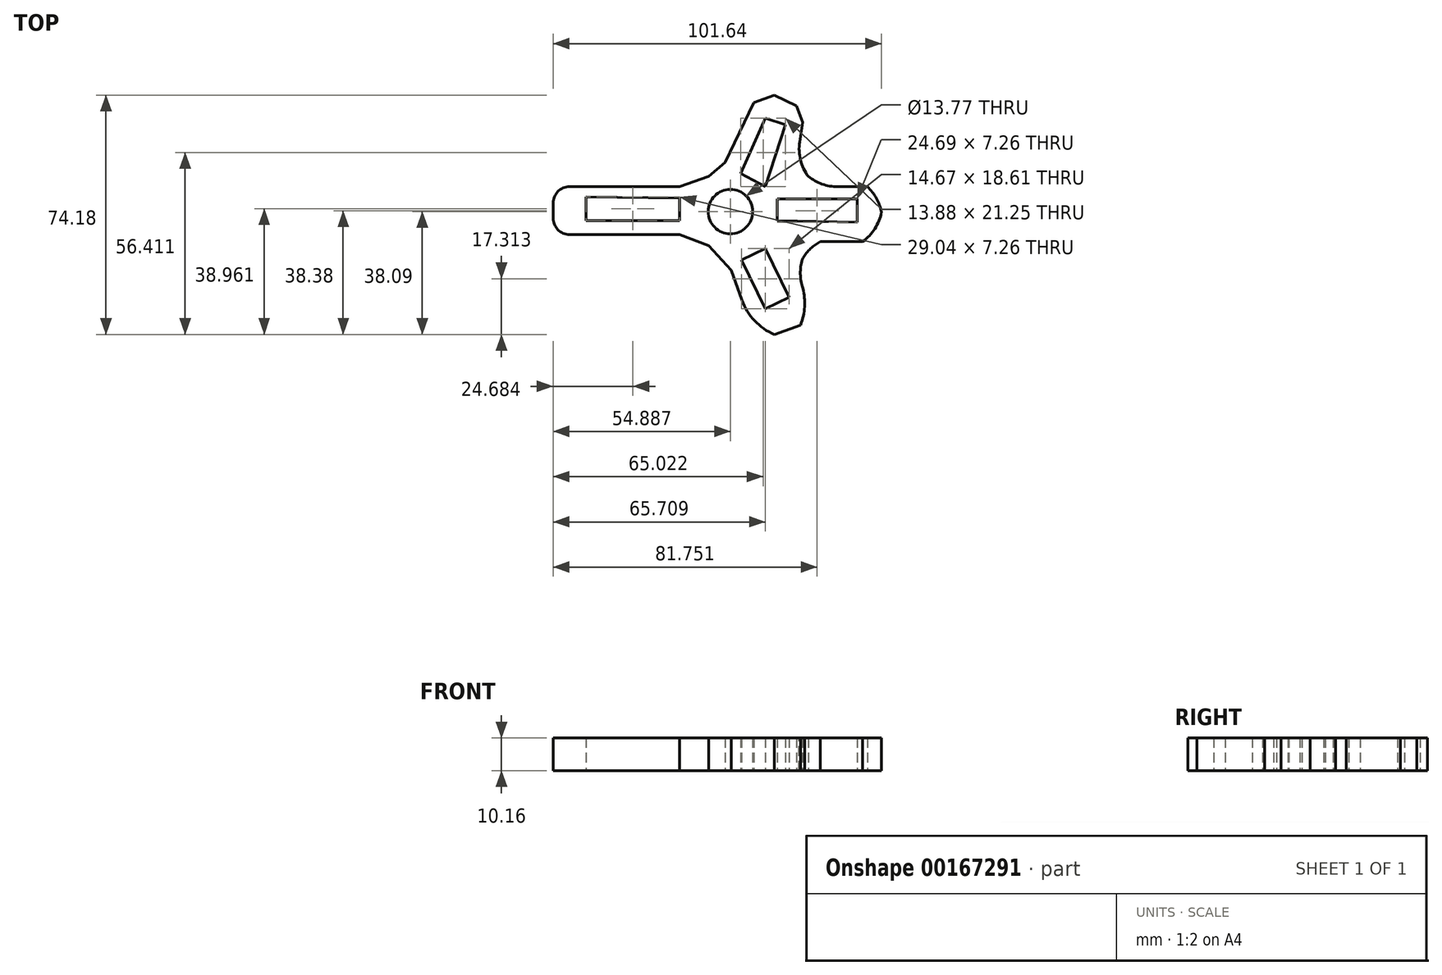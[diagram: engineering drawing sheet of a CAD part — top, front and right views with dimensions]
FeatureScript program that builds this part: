
annotation { "Feature Type Name" : "Feature", "Feature Type Description" : "" }
export const myFeature = defineFeature(function(context is Context, id is Id, definition is map)
    precondition{}
    {
        {
            var Q0;
            Q0=qCreatedBy(makeId("Top.planeOp"),FACE);
            var sketch = newSketch(context, id + "F0", { "sketchPlane" : qUnion([Q0])});
            skLineSegment(sketch, "E0", {"start": v(5.52, 10.9) * mm, "end": v(-3.49, 7.7) * mm});
            skLineSegment(sketch, "E1", {"start": v(-3.49, 7.7) * mm, "end": v(-42.7, 7.7) * mm});
            skLineSegment(sketch, "E2", {"start": v(-42.7, 7.7) * mm, "end": v(-42.7, -7.12) * mm});
            skLineSegment(sketch, "E3", {"start": v(-42.7, -7.12) * mm, "end": v(-3.49, -7.12) * mm});
            skLineSegment(sketch, "E4", {"start": v(-3.49, -7.12) * mm, "end": v(5.52, -10.6) * mm});
            skLineSegment(sketch, "E5", {"start": v(5.52, -10.6) * mm, "end": v(12.49, -18.15) * mm});
            skLineSegment(sketch, "E6", {"start": v(12.49, -18.15) * mm, "end": v(19.56, -38.09) * mm});
            skLineSegment(sketch, "E7", {"start": v(19.56, -38.09) * mm, "end": v(25.85, -38.09) * mm});
            skLineSegment(sketch, "E8", {"start": v(25.85, -38.09) * mm, "end": v(33.86, -35.24) * mm});
            skLineSegment(sketch, "E9", {"start": v(33.86, -35.24) * mm, "end": v(36.3, -28.32) * mm});
            skLineSegment(sketch, "E10", {"start": v(36.3, -28.32) * mm, "end": v(32.7, -18.15) * mm});
            skLineSegment(sketch, "E11", {"start": v(32.7, -18.15) * mm, "end": v(36.3, -10.6) * mm});
            skLineSegment(sketch, "E12", {"start": v(36.3, -10.6) * mm, "end": v(40.05, -9.27) * mm});
            skLineSegment(sketch, "E13", {"start": v(40.05, -9.27) * mm, "end": v(53.15, -9.27) * mm});
            skLineSegment(sketch, "E14", {"start": v(53.15, -9.27) * mm, "end": v(59.22, -7.12) * mm});
            skLineSegment(sketch, "E15", {"start": v(59.22, -7.12) * mm, "end": v(59.22, 5.37) * mm});
            skLineSegment(sketch, "E16", {"start": v(59.22, 5.37) * mm, "end": v(54.6, 7.7) * mm});
            skLineSegment(sketch, "E17", {"start": v(54.6, 7.7) * mm, "end": v(40.05, 7.7) * mm});
            skLineSegment(sketch, "E18", {"start": v(40.05, 7.7) * mm, "end": v(36.3, 10.9) * mm});
            skLineSegment(sketch, "E19", {"start": v(36.3, 10.9) * mm, "end": v(32.7, 15.25) * mm});
            skLineSegment(sketch, "E20", {"start": v(32.7, 15.25) * mm, "end": v(34.5, 27.73) * mm});
            skPoint(sketch, "E20.endSnap0", {"position": v(34.5, -23.23) * mm});
            skLineSegment(sketch, "E21", {"start": v(34.5, 27.73) * mm, "end": v(32.7, 32.82) * mm});
            skLineSegment(sketch, "E22", {"start": v(32.7, 32.82) * mm, "end": v(25.85, 36.09) * mm});
            skLineSegment(sketch, "E23", {"start": v(25.85, 36.09) * mm, "end": v(19.48, 33.83) * mm});
            skLineSegment(sketch, "E24", {"start": v(19.48, 33.83) * mm, "end": v(10.6, 15.25) * mm});
            skLineSegment(sketch, "E25", {"start": v(10.6, 15.25) * mm, "end": v(5.52, 10.9) * mm});
            skLineSegment(sketch, "E26", {"start": v(-32.53, 4.5) * mm, "end": v(-32.53, -2.76) * mm});
            skLineSegment(sketch, "E27", {"start": v(-32.53, -2.76) * mm, "end": v(-3.49, -2.76) * mm});
            skLineSegment(sketch, "E28", {"start": v(-3.49, -2.76) * mm, "end": v(-3.49, 4.21) * mm});
            skLineSegment(sketch, "E29", {"start": v(-3.49, 4.21) * mm, "end": v(-32.53, 4.5) * mm});
            skLineSegment(sketch, "E30", {"start": v(15.4, 11.76) * mm, "end": v(22.94, 7.7) * mm});
            skLineSegment(sketch, "E31", {"start": v(22.94, 7.7) * mm, "end": v(29.27, 26.86) * mm});
            skPoint(sketch, "E31.endSnap0", {"position": v(29.27, 34.45) * mm});
            skLineSegment(sketch, "E32", {"start": v(29.27, 26.86) * mm, "end": v(22.96, 28.95) * mm});
            skLineSegment(sketch, "E33", {"start": v(22.96, 28.95) * mm, "end": v(15.4, 11.76) * mm});
            skLineSegment(sketch, "E34", {"start": v(26.72, -2.76) * mm, "end": v(26.72, 3.92) * mm});
            skLineSegment(sketch, "E35", {"start": v(26.72, 3.92) * mm, "end": v(51.4, 3.92) * mm});
            skLineSegment(sketch, "E36", {"start": v(51.4, 3.92) * mm, "end": v(51.4, -3.34) * mm});
            skLineSegment(sketch, "E37", {"start": v(51.4, -3.34) * mm, "end": v(26.72, -2.76) * mm});
            skLineSegment(sketch, "E38", {"start": v(22.94, -11.47) * mm, "end": v(15.68, -14.96) * mm});
            skLineSegment(sketch, "E39", {"start": v(15.68, -14.96) * mm, "end": v(22.94, -30.08) * mm});
            skLineSegment(sketch, "E40", {"start": v(22.94, -30.08) * mm, "end": v(30.35, -26.52) * mm});
            skLineSegment(sketch, "E41", {"start": v(30.35, -26.52) * mm, "end": v(22.94, -11.47) * mm});
            skCircle(sketch, "E42", {"center": v(12.2, 0) * mm, "radius": 6.89 * mm});
            skSolve(sketch);
        }
        {
            var Q0;
            Q0 = qSketchRegion(id + "F0", true);
            extrude(context, id + "F1", {"entities" : qUnion([Q0]), "depth" : 10.16 * mm});
        }
        {
            var Q0;
            Q0=makeQuery(id+"F1.opExtrude","SWEPT_EDGE",EDGE,{"disambiguationData":[OSD([sQuery(id+"F0.wireOp",EDGE,"E6"),sQuery(id+"F0.wireOp",EDGE,"E7")])]});
            var Q1;
            Q1=makeQuery(id+"F1.opExtrude","SWEPT_EDGE",EDGE,{"disambiguationData":[OSD([sQuery(id+"F0.wireOp",EDGE,"E9"),sQuery(id+"F0.wireOp",EDGE,"E10")])]});
            fillet(context, id + "F2", {"entities" : qUnion([Q0, Q1]), "radius" : 18.12 * mm, "tangentPropagation" : true, "allowEdgeOverflow" : false});
        }
        {
            var Q0;
            Q0=makeQuery(id+"F1.opExtrude","SWEPT_EDGE",EDGE,{"disambiguationData":[OSD([sQuery(id+"F0.wireOp",EDGE,"E19"),sQuery(id+"F0.wireOp",EDGE,"E20")])]});
            var Q1;
            Q1=makeQuery(id+"F1.opExtrude","SWEPT_EDGE",EDGE,{"disambiguationData":[OSD([sQuery(id+"F0.wireOp",EDGE,"E17"),sQuery(id+"F0.wireOp",EDGE,"E18")])]});
            var Q2;
            Q2=makeQuery(id+"F1.opExtrude","SWEPT_EDGE",EDGE,{"disambiguationData":[OSD([sQuery(id+"F0.wireOp",EDGE,"E10"),sQuery(id+"F0.wireOp",EDGE,"E11")])]});
            var Q3;
            Q3=makeQuery(id+"F1.opExtrude","SWEPT_EDGE",EDGE,{"disambiguationData":[OSD([sQuery(id+"F0.wireOp",EDGE,"E11"),sQuery(id+"F0.wireOp",EDGE,"E12")])]});
            var Q4;
            Q4=makeQuery(id+"F1.opExtrude","SWEPT_EDGE",EDGE,{"disambiguationData":[OSD([sQuery(id+"F0.wireOp",EDGE,"E14"),sQuery(id+"F0.wireOp",EDGE,"E15")])]});
            var Q5;
            Q5=makeQuery(id+"F1.opExtrude","SWEPT_EDGE",EDGE,{"disambiguationData":[OSD([sQuery(id+"F0.wireOp",EDGE,"E15"),sQuery(id+"F0.wireOp",EDGE,"E16")])]});
            fillet(context, id + "F3", {"entities" : qUnion([Q0, Q1, Q2, Q3, Q4, Q5]), "radius" : 14.55 * mm, "tangentPropagation" : true, "allowEdgeOverflow" : false});
        }
        {
            var Q0;
            Q0=makeQuery(id+"F1.opExtrude","SWEPT_EDGE",EDGE,{"disambiguationData":[OSD([sQuery(id+"F0.wireOp",EDGE,"E1"),sQuery(id+"F0.wireOp",EDGE,"E2")])]});
            var Q1;
            Q1=makeQuery(id+"F1.opExtrude","SWEPT_EDGE",EDGE,{"disambiguationData":[OSD([sQuery(id+"F0.wireOp",EDGE,"E2"),sQuery(id+"F0.wireOp",EDGE,"E3")])]});
            fillet(context, id + "F4", {"entities" : qUnion([Q0, Q1]), "radius" : 5.08 * mm, "tangentPropagation" : true, "allowEdgeOverflow" : false});
        }
    });
